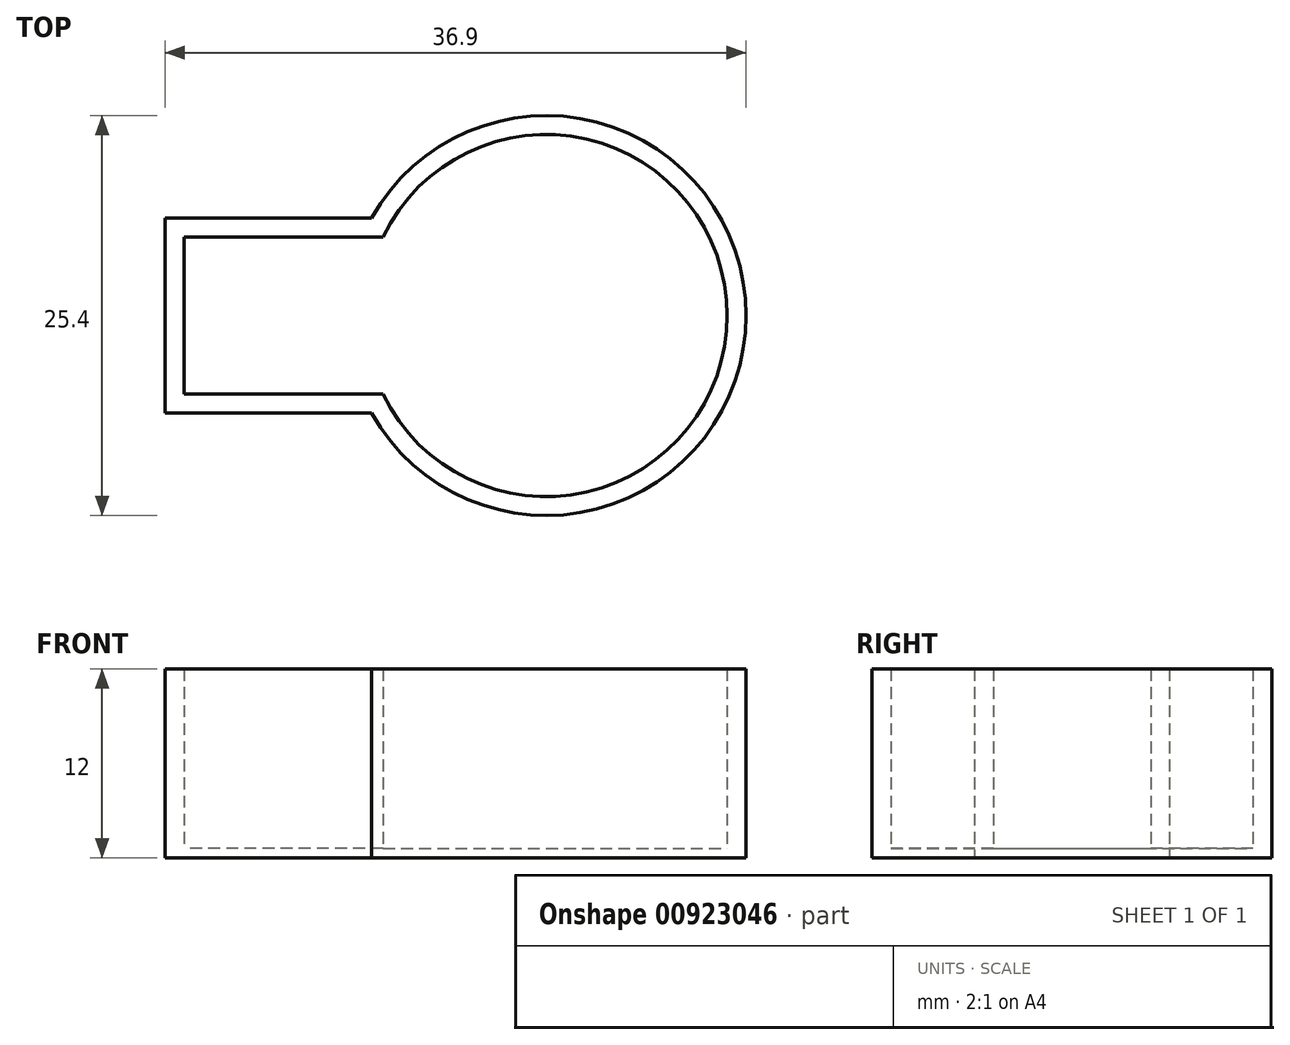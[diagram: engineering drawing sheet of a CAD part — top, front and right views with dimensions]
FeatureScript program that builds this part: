
annotation { "Feature Type Name" : "Feature", "Feature Type Description" : "" }
export const myFeature = defineFeature(function(context is Context, id is Id, definition is map)
    precondition{}
    {
        {
            var Q0;
            Q0=qCreatedBy(makeId("Top.planeOp"),FACE);
            var sketch = newSketch(context, id + "F0", { "sketchPlane" : qUnion([Q0])});
            skCircle(sketch, "E0", {"center": v(0, 0) * mm, "radius": 11.5 * mm});
            skLineSegment(sketch, "E1.bottom", {"start": v(0, 0) * mm, "end": v(-23, 0) * mm});
            skLineSegment(sketch, "E1.top", {"start": v(0, 5) * mm, "end": v(-23, 5) * mm});
            skLineSegment(sketch, "E1.left", {"start": v(0, 0) * mm, "end": v(0, 5) * mm});
            skLineSegment(sketch, "E1.right", {"start": v(-23, 0) * mm, "end": v(-23, 5) * mm});
            skLineSegment(sketch, "E2.MirrorCS", {"start": v(0, -5) * mm, "end": v(-23, -5) * mm});
            skLineSegment(sketch, "E3.MirrorCS", {"start": v(-23, 0) * mm, "end": v(-23, -5) * mm});
            skCircle(sketch, "E4.0", {"center": v(0, 0) * mm, "radius": 12.7 * mm});
            skLineSegment(sketch, "E5.0", {"start": v(0, -6.2) * mm, "end": v(-24.2, -6.2) * mm});
            skLineSegment(sketch, "E5.1", {"start": v(-24.2, 0) * mm, "end": v(-24.2, -6.2) * mm});
            skLineSegment(sketch, "E5.2", {"start": v(-24.2, 0) * mm, "end": v(-24.2, 6.2) * mm});
            skLineSegment(sketch, "E5.3", {"start": v(0, 6.2) * mm, "end": v(-24.2, 6.2) * mm});
            skSolve(sketch);
        }
        {
            var Q0;
            {var subQ4=sQuery(id+"F0.wireOp",EDGE,"E1.right");Q0=makeQuery(id+"F0.imprint","IMPRINT",FACE,{"disambiguationData":[TD([[makeQuery(id+"F0.imprint","IMPRINT",EDGE,{"derivedFrom":subQ4}),1.0]])]});}
            var Q1;
            {var subQ0=sQuery(id+"F0.wireOp",EDGE,"E5.3");var subQ1=sQuery(id+"F0.wireOp",EDGE,"E0");var subQ2=makeQuery(id+"F0.imprint","INTERSECT",VERTEX,{"derivedFrom":[subQ1,subQ0]});Q1=makeQuery(id+"F0.imprint","IMPRINT",FACE,{"disambiguationData":[TD([[makeQuery(id+"F0.imprint","IMPRINT",EDGE,{"disambiguationData":[TD([[subQ2,1.0]])],"derivedFrom":subQ1}),-1.0]])]});}
            var Q2;
            {var subQ0=sQuery(id+"F0.wireOp",EDGE,"E5.3");var subQ1=sQuery(id+"F0.wireOp",EDGE,"E0");var subQ2=makeQuery(id+"F0.imprint","INTERSECT",VERTEX,{"derivedFrom":[subQ1,subQ0]});Q2=makeQuery(id+"F0.imprint","IMPRINT",FACE,{"disambiguationData":[TD([[makeQuery(id+"F0.imprint","IMPRINT",EDGE,{"disambiguationData":[TD([[subQ2,-1.0]])],"derivedFrom":subQ1}),-1.0]])]});}
            var Q3;
            {var subQ0=sQuery(id+"F0.wireOp",EDGE,"E2.MirrorCS");var subQ1=sQuery(id+"F0.wireOp",EDGE,"E0");var subQ2=makeQuery(id+"F0.imprint","INTERSECT",VERTEX,{"derivedFrom":[subQ1,subQ0]});Q3=makeQuery(id+"F0.imprint","IMPRINT",FACE,{"disambiguationData":[TD([[makeQuery(id+"F0.imprint","IMPRINT",EDGE,{"disambiguationData":[TD([[subQ2,-1.0]])],"derivedFrom":subQ1}),-1.0]])]});}
            extrude(context, id + "F1", {"entities" : qUnion([Q0, Q1, Q2, Q3]), "depth" : 12 * mm, "offsetDistance" : 25 * mm});
        }
        {
            var Q0;
            {var subQ8=sQuery(id+"F0.wireOp",EDGE,"E1.left");Q0=makeQuery(id+"F0.imprint","IMPRINT",FACE,{"disambiguationData":[TD([[makeQuery(id+"F0.imprint","IMPRINT",EDGE,{"derivedFrom":subQ8}),-1.0]])]});}
            var Q1;
            {var subQ0=sQuery(id+"F0.wireOp",EDGE,"E1.right");Q1=makeQuery(id+"F0.imprint","IMPRINT",FACE,{"disambiguationData":[TD([[makeQuery(id+"F0.imprint","IMPRINT",EDGE,{"derivedFrom":subQ0}),-1.0]])]});}
            var Q2;
            {var subQ5=sQuery(id+"F0.wireOp",EDGE,"E1.left");Q2=makeQuery(id+"F0.imprint","IMPRINT",FACE,{"disambiguationData":[TD([[makeQuery(id+"F0.imprint","IMPRINT",EDGE,{"derivedFrom":subQ5}),1.0]])]});}
            var Q3;
            {var subQ0=sQuery(id+"F0.wireOp",EDGE,"E1.top");var subQ1=sQuery(id+"F0.wireOp",EDGE,"E0");var subQ2=makeQuery(id+"F0.imprint","INTERSECT",VERTEX,{"derivedFrom":[subQ1,subQ0]});Q3=makeQuery(id+"F0.imprint","IMPRINT",FACE,{"disambiguationData":[TD([[makeQuery(id+"F0.imprint","IMPRINT",EDGE,{"disambiguationData":[TD([[subQ2,-1.0]])],"derivedFrom":subQ1}),-1.0]])]});}
            var Q4;
            {var subQ0=sQuery(id+"F0.wireOp",EDGE,"E3.MirrorCS");Q4=makeQuery(id+"F0.imprint","IMPRINT",FACE,{"disambiguationData":[TD([[makeQuery(id+"F0.imprint","IMPRINT",EDGE,{"derivedFrom":subQ0}),1.0]])]});}
            var Q5;
            {var subQ0=sQuery(id+"F0.wireOp",EDGE,"E2.MirrorCS");var subQ1=sQuery(id+"F0.wireOp",EDGE,"E0");var subQ2=makeQuery(id+"F0.imprint","INTERSECT",VERTEX,{"derivedFrom":[subQ1,subQ0]});Q5=makeQuery(id+"F0.imprint","IMPRINT",FACE,{"disambiguationData":[TD([[makeQuery(id+"F0.imprint","IMPRINT",EDGE,{"disambiguationData":[TD([[subQ2,1.0]])],"derivedFrom":subQ1}),-1.0]])]});}
            extrude(context, id + "F2", {"entities" : qUnion([Q0, Q1, Q2, Q3, Q4, Q5]), "operationType" : NewBodyOperationType.ADD, "depth" : 0.6 * mm, "offsetDistance" : 25 * mm});
        }
    });
